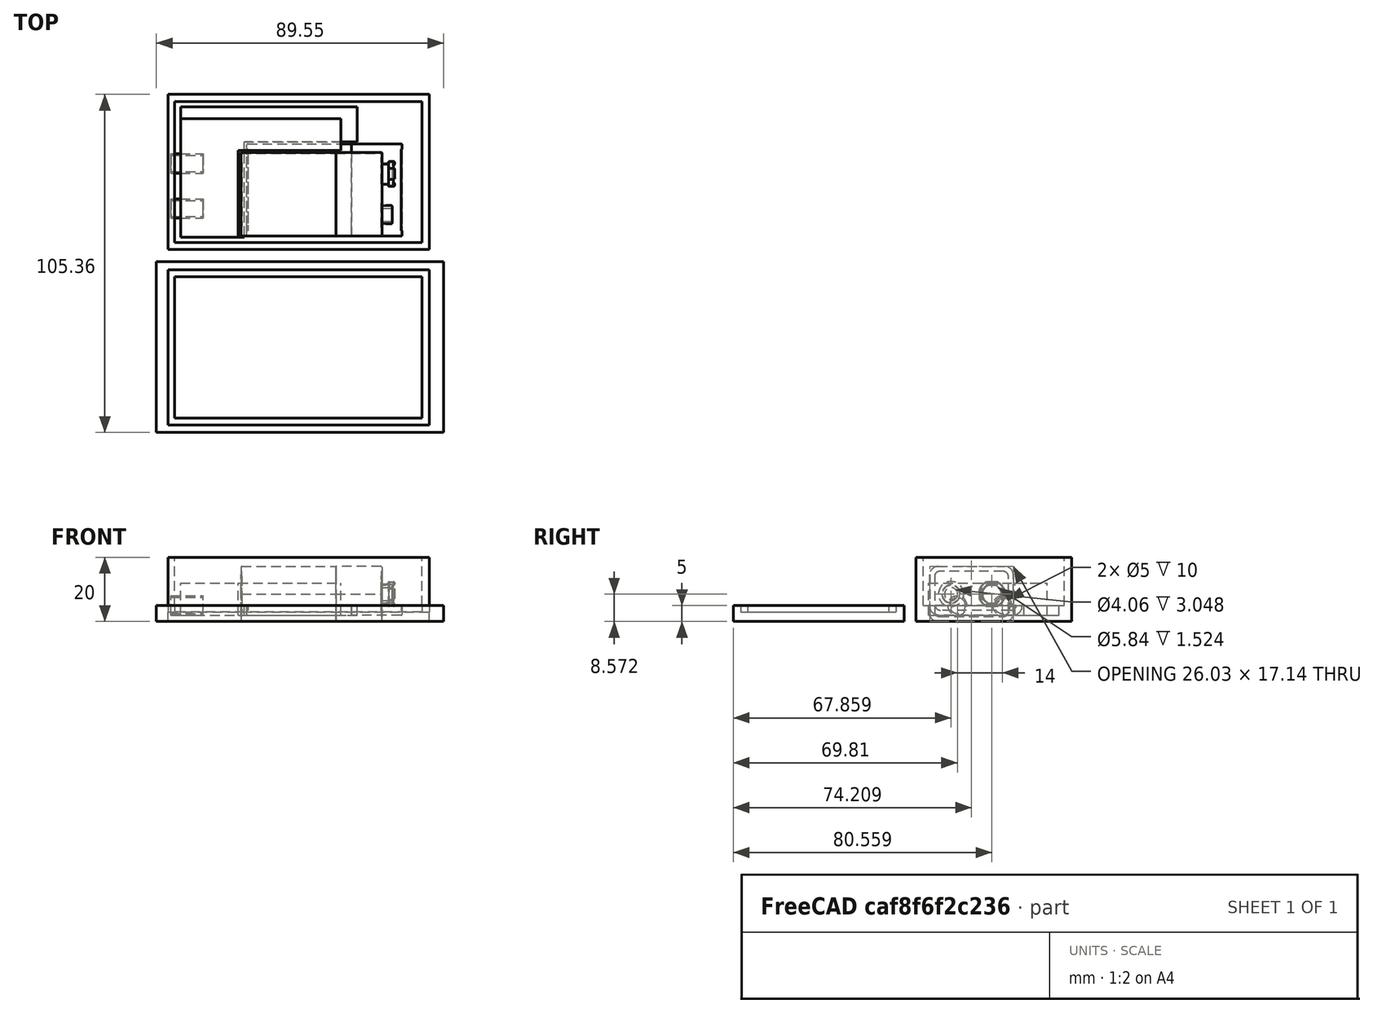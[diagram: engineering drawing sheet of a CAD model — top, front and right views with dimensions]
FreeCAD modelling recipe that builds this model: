
FCSTD DOCUMENT  (FreeCAD 0.18R13548 (Git))
Label: cmoy
License: All rights reserved
LicenseURL: http://en.wikipedia.org/wiki/All_rights_reserved
objects: Part::Cut×7, Part::Cylinder×4, Part::MultiFuse×3, Part::Part2DObjectPython×3, Part::Extrusion×3, Part::FeaturePython×3, Part::Feature×2, Part::Box×2, Spreadsheet::Sheet×1
note: 27 computed .brp shape members not serialized (recipe doc carries the construction recipe); baked Part::Feature solids carry a one-line shape summary decoded from their .brp

FEATURE [Part::Feature] Part__Feature  label="layer1[1]"
  Placement = pos=(108,33.5,0) rot=(0,0,1;1.5708rad)
  shape: bbox 47.88 x 26.45 x 17.56 mm, 192 faces (baked)
FEATURE [Part::Box] Box  label="Cubo"
  AttacherType = Attacher::AttachEngine3D
  Height = 10
  Length = 18
  Width = 37
  expr: Height = Spreadsheet.h_cmoy
FEATURE [Spreadsheet::Sheet] Spreadsheet
  cells = B3=h_cmoy; C3(h_cmoy)=10
FEATURE [Part::Box] Box001  label="Cubo001"
  AttacherType = Attacher::AttachEngine3D
  Height = 10
  Length = 32
  Placement = pos=(18,27,0) rot=(0,0,1;0rad)
  Width = 10
  expr: Height = Spreadsheet.h_cmoy
FEATURE [Part::MultiFuse] Fusion  label="base"
  Placement = pos=(0,0,2) rot=(0,0,1;0rad)
  Shapes = -> [Box,Box001]
FEATURE [Part::Cylinder] Cylinder  label="Cilindro"
  Angle = 360
  AttacherType = Attacher::AttachEngine3D
  Height = 10
  Placement = pos=(-3,9,5) rot=(0,1,0;1.5708rad)
  Radius = 2.5
FEATURE [Part::Cylinder] Cylinder001  label="Cilindro001"
  Angle = 360
  AttacherType = Attacher::AttachEngine3D
  Height = 10
  Placement = pos=(-3,23,5) rot=(0,1,0;1.5708rad)
  Radius = 2.5
FEATURE [Part::Cylinder] Cylinder002  label="Cilindro002"
  Angle = 360
  AttacherType = Attacher::AttachEngine3D
  Height = 10
  Placement = pos=(-3,9,5) rot=(0,1,0;1.5708rad)
  Radius = 3
FEATURE [Part::Cylinder] Cylinder003  label="Cilindro003"
  Angle = 360
  AttacherType = Attacher::AttachEngine3D
  Height = 10
  Placement = pos=(-3,23,5) rot=(0,1,0;1.5708rad)
  Radius = 3
FEATURE [Part::Cut] Cut
  Base = -> Cylinder003
  Tool = -> Cylinder001
FEATURE [Part::Cut] Cut001
  Base = -> Cylinder002
  Tool = -> Cylinder
FEATURE [Part::MultiFuse] Fusion001  label="jacks"
  Shapes = -> [Cut,Cut001]
FEATURE [Part::Part2DObjectPython] DWire  # Draft 2D object (typed FeaturePython)
  ChamferSize = 0
  Closed = true
  End = (-3.5,-3.5,0)
  FilletRadius = 0
  Length = 236
  MakeFace = true
  Points = (4) [(-3.5,40.5,0),(70.5,40.5,0),(70.5,-3.5,0),(-3.5,-3.5,0)]
  Start = (-3.5,40.5,0)
  Subdivisions = 0
FEATURE [Part::Part2DObjectPython] DWire001  # Draft 2D object (typed FeaturePython)
  ChamferSize = 0
  Closed = true
  End = (68.3601,38.5023,2)
  FilletRadius = 0
  Length = 220
  MakeFace = true
  Placement = pos=(0,0,2) rot=(0,0,1;0rad)
  Points = (4) [(-1.63991,38.5023,0),(-1.63991,-1.49768,0),(68.3601,-1.49768,0),(68.3601,38.5023,0)]
  Start = (-1.63991,38.5023,2)
  Subdivisions = 0
FEATURE [Part::Extrusion] Extrude
  Base = -> DWire
  Dir = (0,0,1)
  DirMode = 2
  FaceMakerClass = Part::FaceMakerBullseye
  LengthFwd = 20
  LengthRev = 0
  Solid = true
  Symmetric = false
FEATURE [Part::Part2DObjectPython] DWire002  # Draft 2D object (typed FeaturePython)
  ChamferSize = 0
  Closed = true
  End = (68.3601,38.5023,2)
  FilletRadius = 0
  Length = 220
  MakeFace = true
  Placement = pos=(0,0,2) rot=(0,0,1;0rad)
  Points = (4) [(-1.63991,38.5023,0),(-1.63991,-1.49768,0),(68.3601,-1.49768,0),(68.3601,38.5023,0)]
  Start = (-1.63991,38.5023,2)
  Subdivisions = 0
FEATURE [Part::Extrusion] Extrude001
  Base = -> DWire001
  Dir = (0,0,1)
  DirMode = 2
  FaceMakerClass = Part::FaceMakerBullseye
  LengthFwd = 20
  LengthRev = 0
  Placement = pos=(0,0,3) rot=(0,0,1;0rad)
  Solid = false
  Symmetric = false
FEATURE [Part::Cut] Cut002
  Base = -> Extrude
  Tool = -> Extrude001
FEATURE [Part::MultiFuse] Fusion002  label="base001"
  Placement = pos=(0,0,2) rot=(0,0,1;0rad)
  Shapes = -> [Box,Box001]
FEATURE [Part::Cut] Cut003
  Base = -> Cut002
  Tool = -> Fusion002
FEATURE [Part::Feature] Part__Feature001  label="layer1[1]001"
  Placement = pos=(108,33.5,2) rot=(0,0,1;1.5708rad)
  shape: bbox 47.88 x 26.45 x 17.56 mm, 192 faces (baked)
FEATURE [Part::Cut] Cut004
  Base = -> Cut003
  Tool = -> Part__Feature001
FEATURE [Part::Extrusion] Extrude002
  Base = -> DWire
  Dir = (0,0,1)
  DirMode = 2
  FaceMakerClass = Part::FaceMakerBullseye
  LengthFwd = 5
  LengthRev = 0
  Placement = pos=(0,0,18) rot=(0,0,1;0rad)
  Solid = true
  Symmetric = false
FEATURE [Part::Cut] Cut005
  Base = -> Cut003
  Tool = -> Part__Feature001
FEATURE [Part::FeaturePython] Clone  label="Extrude003"  # Draft clone (typed FeaturePython)
  AttacherType = Attacher::AttachEngine3D
  Fuse = false
  Objects = -> [Extrude002]
  Placement = pos=(-3,-2,18) rot=(0,0,1;0rad)
  Scale = (1.1,1.1,1)
FEATURE [Part::Cut] Cut006
  Base = -> Clone
  Placement = pos=(0,-14,23) rot=(1,0,0;3.14159rad)
  Tool = -> Cut005
FEATURE [Part::FeaturePython] Clone001  label="Cut007"  # Draft clone (typed FeaturePython)
  AttacherType = Attacher::AttachEngine3D
  Fuse = false
  Objects = -> [Cut004]
  Scale = (1.1,1.1,1)
FEATURE [Part::FeaturePython] Clone002  label="Cut008"  # Draft clone (typed FeaturePython)
  AttacherType = Attacher::AttachEngine3D
  Fuse = false
  Objects = -> [Cut006]
  Placement = pos=(0,-14,23) rot=(1,0,0;3.14159rad)
  Scale = (1.1,1.1,1)
